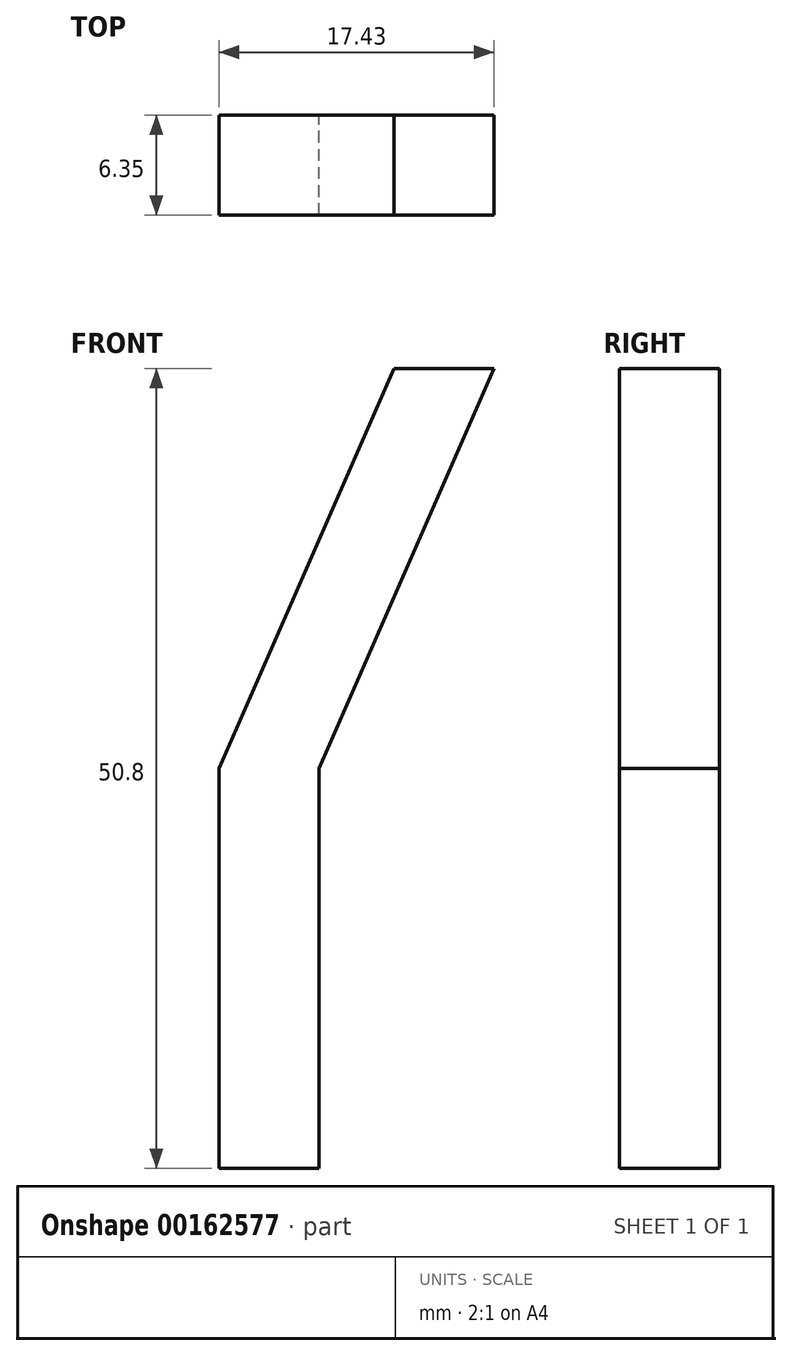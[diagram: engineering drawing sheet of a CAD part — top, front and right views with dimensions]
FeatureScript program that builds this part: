
annotation { "Feature Type Name" : "Feature", "Feature Type Description" : "" }
export const myFeature = defineFeature(function(context is Context, id is Id, definition is map)
    precondition{}
    {
        {
            var Q0;
            Q0=qCreatedBy(makeId("Front.planeOp"),FACE);
            var sketch = newSketch(context, id + "F0", { "sketchPlane" : qUnion([Q0])});
            skLineSegment(sketch, "E0.bottom", {"start": v(0, 0) * mm, "end": v(6.35, 0) * mm});
            skLineSegment(sketch, "E0.top", {"start": v(0, 25.4) * mm, "end": v(6.35, 25.4) * mm});
            skLineSegment(sketch, "E0.left", {"start": v(0, 0) * mm, "end": v(0, 25.4) * mm});
            skLineSegment(sketch, "E0.right", {"start": v(6.35, 0) * mm, "end": v(6.35, 25.4) * mm});
            skLineSegment(sketch, "E1", {"start": v(0, 25.4) * mm, "end": v(11.08, 50.8) * mm});
            skLineSegment(sketch, "E2", {"start": v(6.35, 25.4) * mm, "end": v(17.43, 50.8) * mm});
            skLineSegment(sketch, "E3", {"start": v(17.43, 50.8) * mm, "end": v(11.08, 50.8) * mm});
            skSolve(sketch);
        }
        {
            var Q0;
            Q0 = qSketchRegion(id + "F0", true);
            extrude(context, id + "F1", {"entities" : qUnion([Q0]), "depth" : 6.35 * mm});
        }
    });
